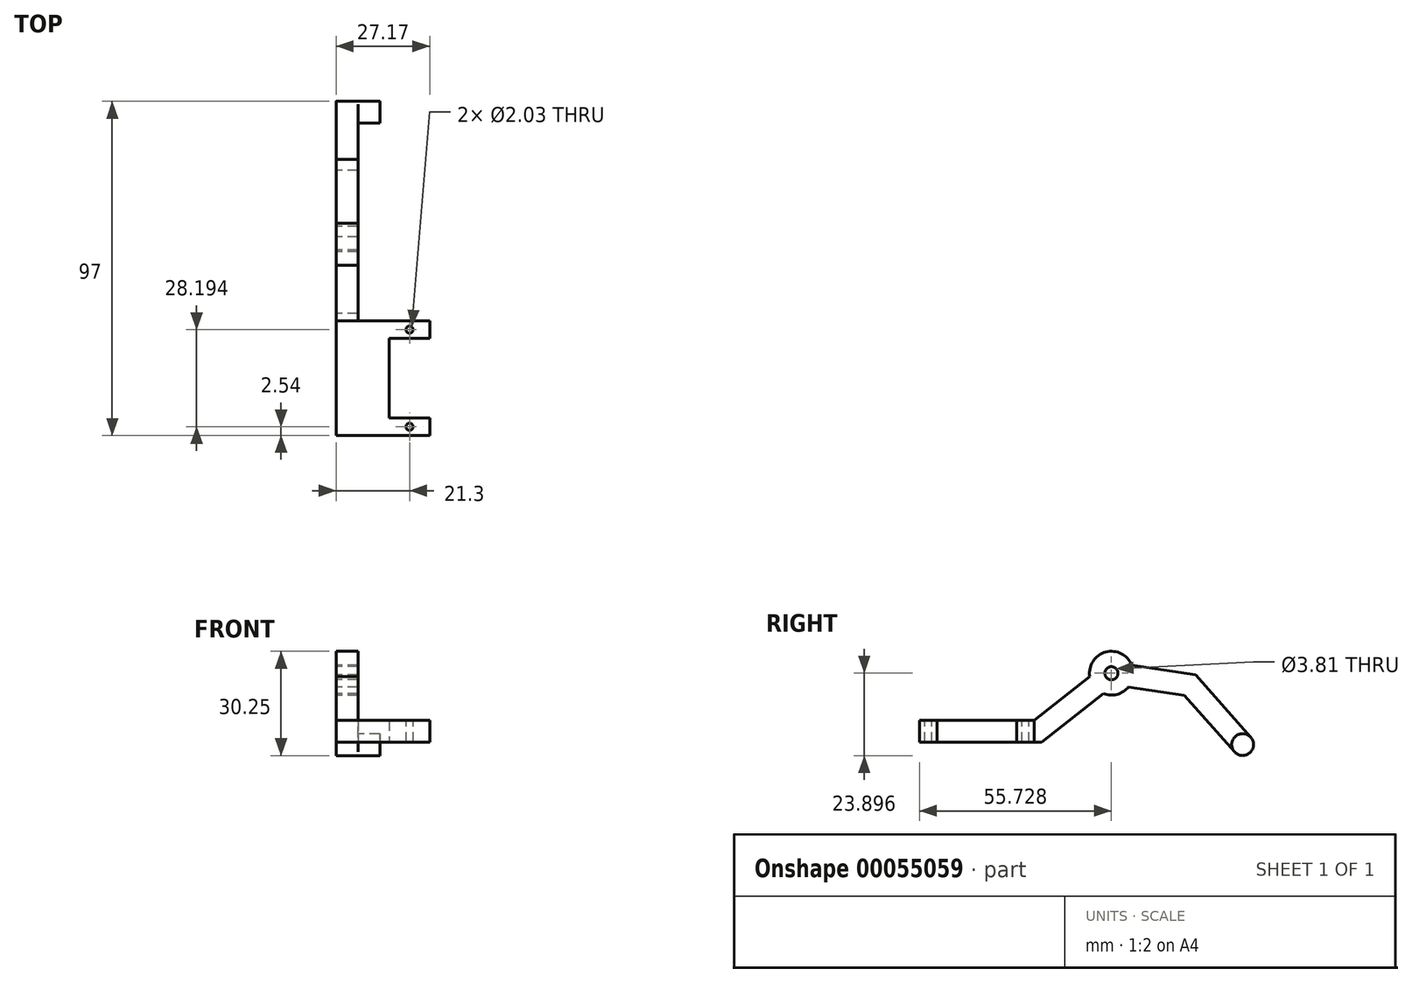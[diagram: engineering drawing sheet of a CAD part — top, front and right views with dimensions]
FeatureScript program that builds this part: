
annotation { "Feature Type Name" : "Feature", "Feature Type Description" : "" }
export const myFeature = defineFeature(function(context is Context, id is Id, definition is map)
    precondition{}
    {
        {
            var Q0;
            Q0=qCreatedBy(makeId("Right.planeOp"),FACE);
            var sketch = newSketch(context, id + "F0", { "sketchPlane" : qUnion([Q0])});
            skLineSegment(sketch, "E0", {"start": v(0, 0) * mm, "end": v(0, 6.35) * mm});
            skLineSegment(sketch, "E1", {"start": v(0, 0) * mm, "end": v(35.48, 0) * mm});
            skLineSegment(sketch, "E2", {"start": v(35.48, 0) * mm, "end": v(53.38, 14.16) * mm});
            skArc(sketch, "E3", {"start": v(53.38, 14.16) * mm, "mid": v(57.36, 13.93) * mm, "end": v(60.7, 16.11) * mm});
            skLineSegment(sketch, "E4", {"start": v(0, 6.35) * mm, "end": v(33.27, 6.35) * mm});
            skLineSegment(sketch, "E5", {"start": v(33.27, 6.35) * mm, "end": v(49.44, 19.14) * mm});
            skLineSegment(sketch, "E6", {"start": v(60.7, 16.11) * mm, "end": v(76.93, 13.67) * mm});
            skLineSegment(sketch, "E7", {"start": v(91.45, -2.75) * mm, "end": v(76.93, 13.67) * mm});
            skArc(sketch, "E8", {"start": v(91.45, -2.75) * mm, "mid": v(95.93, -3.03) * mm, "end": v(96.2, 1.45) * mm});
            skLineSegment(sketch, "E9", {"start": v(61.64, 22.39) * mm, "end": v(80.16, 19.6) * mm});
            skLineSegment(sketch, "E10", {"start": v(96.2, 1.45) * mm, "end": v(80.16, 19.6) * mm});
            skArc(sketch, "E11.trimOffspring", {"start": v(61.64, 22.39) * mm, "mid": v(54.1, 26.2) * mm, "end": v(49.44, 19.14) * mm});
            skLineSegment(sketch, "E12", {"start": v(5.08, 6.35) * mm, "end": v(5.08, 0) * mm, "construction": true});
            skLineSegment(sketch, "E13", {"start": v(28.2, 6.35) * mm, "end": v(28.2, 0) * mm, "construction": true});
            skLineSegment(sketch, "E14", {"start": v(55.73, 20.07) * mm, "end": v(78.55, 16.64) * mm, "construction": true});
            skLineSegment(sketch, "E15", {"start": v(78.55, 16.64) * mm, "end": v(93.83, -0.65) * mm, "construction": true});
            skLineSegment(sketch, "E16", {"start": v(60.7, 16.11) * mm, "end": v(61.64, 22.39) * mm, "construction": true});
            skPoint(sketch, "E17", {"position": v(61.17, 19.25) * mm});
            skLineSegment(sketch, "E18", {"start": v(91.45, -2.75) * mm, "end": v(96.2, 1.45) * mm, "construction": true});
            skLineSegment(sketch, "E19", {"start": v(49.44, 19.14) * mm, "end": v(53.38, 14.16) * mm, "construction": true});
            skLineSegment(sketch, "E20", {"start": v(51.41, 16.65) * mm, "end": v(55.73, 20.07) * mm, "construction": true});
            skCircle(sketch, "E21", {"center": v(55.73, 20.07) * mm, "radius": 1.9 * mm});
            skSolve(sketch);
        }
        {
            var Q0;
            Q0=makeQuery(id+"F0.imprint","IMPRINT",FACE,{"disambiguationData":[TD([[makeQuery(id+"F0.imprint","IMPRINT",EDGE,{"derivedFrom":sQuery(id+"F0.wireOp",EDGE,"E0")}),-1.0]])]});
            extrude(context, id + "F1", {"entities" : qUnion([Q0]), "depth" : 6.35 * mm});
        }
        {
            var Q0;
            {var subQ0=sQuery(id+"F0.wireOp",EDGE,"E9");var subQ1=sQuery(id+"F0.wireOp",EDGE,"E7");var subQ2=sQuery(id+"F0.wireOp",EDGE,"E6");var subQ3=sQuery(id+"F0.wireOp",EDGE,"E5");var subQ4=sQuery(id+"F0.wireOp",EDGE,"E8");var subQ5=sQuery(id+"F0.wireOp",EDGE,"E1");var subQ6=sQuery(id+"F0.wireOp",EDGE,"E2");var subQ7=sQuery(id+"F0.wireOp",EDGE,"E10");var subQ8=sQuery(id+"F0.wireOp",EDGE,"E3");var subQ9=sQuery(id+"F0.wireOp",EDGE,"E4");var subQ10=sQuery(id+"F0.wireOp",EDGE,"E11.trimOffspring");Q0=makeQuery(id+"FnFxDPICjbSdQn6_1.boolean.opBoolean","SPLIT",FACE,{"disambiguationData":[TD([makeQuery(id+"F1.opExtrude","SWEPT_FACE",FACE,{"disambiguationData":[OSD([subQ6])]})])],"derivedFrom":makeQuery(id+"F1.opExtrude","CAP_FACE",FACE,{"disambiguationData":[OSD([sQuery(id+"F0.wireOp",EDGE,"E0"),subQ5,subQ6,subQ8,subQ9,subQ3,subQ2,subQ1,subQ4,subQ0,subQ7,subQ10])],"isStart":false})});}
            var sketch = newSketch(context, id + "F2", { "sketchPlane" : qUnion([Q0])});
            skCircle(sketch, "E22", {"center": v(93.83, -0.65) * mm, "radius": 3.18 * mm});
            skSolve(sketch);
        }
        {
            var Q0;
            Q0 = qSketchRegion(id + "F2", true);
            extrude(context, id + "F3", {"entities" : qUnion([Q0]), "operationType" : NewBodyOperationType.ADD, "depth" : 6.35 * mm});
        }
        {
            var Q0;
            Q0=makeQuery(id+"F1.opExtrude","CAP_FACE",FACE,{"disambiguationData":[OSD([sQuery(id+"F0.wireOp",EDGE,"E0"),sQuery(id+"F0.wireOp",EDGE,"E1"),sQuery(id+"F0.wireOp",EDGE,"E2"),sQuery(id+"F0.wireOp",EDGE,"E3"),sQuery(id+"F0.wireOp",EDGE,"E4"),sQuery(id+"F0.wireOp",EDGE,"E5"),sQuery(id+"F0.wireOp",EDGE,"E6"),sQuery(id+"F0.wireOp",EDGE,"E7"),sQuery(id+"F0.wireOp",EDGE,"E8"),sQuery(id+"F0.wireOp",EDGE,"E9"),sQuery(id+"F0.wireOp",EDGE,"E10"),sQuery(id+"F0.wireOp",EDGE,"E11.trimOffspring"),sQuery(id+"F0.wireOp",EDGE,"E21")])],"isStart":false});
            var sketch = newSketch(context, id + "F4", { "sketchPlane" : qUnion([Q0])});
            skLineSegment(sketch, "E23.bottom", {"start": v(0, 6.35) * mm, "end": v(33.27, 6.35) * mm});
            skLineSegment(sketch, "E23.top", {"start": v(0, 0) * mm, "end": v(33.27, 0) * mm});
            skLineSegment(sketch, "E23.left", {"start": v(0, 6.35) * mm, "end": v(0, 0) * mm});
            skLineSegment(sketch, "E23.right", {"start": v(33.27, 6.35) * mm, "end": v(33.27, 0) * mm});
            skSolve(sketch);
        }
        {
            var Q0;
            Q0=makeQuery(id+"F4.imprint","IMPRINT",FACE,{"disambiguationData":[TD([[makeQuery(id+"F4.imprint","IMPRINT",EDGE,{"derivedFrom":sQuery(id+"F4.wireOp",EDGE,"E23.bottom")}),-1.0]])]});
            extrude(context, id + "F5", {"entities" : qUnion([Q0]), "operationType" : NewBodyOperationType.ADD, "depth" : 9.08 * mm});
        }
        {
            var Q0;
            Q0=makeQuery(id+"F5.opExtrude","CAP_FACE",FACE,{"disambiguationData":[OSD([sQuery(id+"F4.wireOp",EDGE,"E23.bottom"),sQuery(id+"F4.wireOp",EDGE,"E23.top"),sQuery(id+"F4.wireOp",EDGE,"E23.left"),sQuery(id+"F4.wireOp",EDGE,"E23.right")])],"isStart":false});
            var sketch = newSketch(context, id + "F6", { "sketchPlane" : qUnion([Q0])});
            skLineSegment(sketch, "E24.bottom", {"start": v(0, 6.35) * mm, "end": v(5.08, 6.35) * mm});
            skLineSegment(sketch, "E24.top", {"start": v(0, 0) * mm, "end": v(5.08, 0) * mm});
            skLineSegment(sketch, "E24.left", {"start": v(0, 6.35) * mm, "end": v(0, 0) * mm});
            skLineSegment(sketch, "E24.right", {"start": v(5.08, 6.35) * mm, "end": v(5.08, 0) * mm});
            skLineSegment(sketch, "E25.bottom", {"start": v(28.2, 6.35) * mm, "end": v(33.27, 6.35) * mm});
            skLineSegment(sketch, "E25.top", {"start": v(28.2, 0) * mm, "end": v(33.27, 0) * mm});
            skLineSegment(sketch, "E25.left", {"start": v(28.2, 6.35) * mm, "end": v(28.2, 0) * mm});
            skLineSegment(sketch, "E25.right", {"start": v(33.27, 6.35) * mm, "end": v(33.27, 0) * mm});
            skSolve(sketch);
        }
        {
            var Q0;
            Q0 = qSketchRegion(id + "F6", true);
            extrude(context, id + "F7", {"entities" : qUnion([Q0]), "operationType" : NewBodyOperationType.ADD, "depth" : 11.73 * mm});
        }
        {
            var Q0;
            Q0=makeQuery(id+"F7.boolean.opBoolean","MERGE",FACE,{"derivedFrom":[makeQuery(id+"F5.boolean.opBoolean","MERGE",FACE,{"derivedFrom":[makeQuery(id+"F1.opExtrude","SWEPT_FACE",FACE,{"disambiguationData":[OSD([sQuery(id+"F0.wireOp",EDGE,"E4")])]}),makeQuery(id+"F5.opExtrude","SWEPT_FACE",FACE,{"disambiguationData":[OSD([sQuery(id+"F4.wireOp",EDGE,"E23.bottom")])]})]}),makeQuery(id+"F7.opExtrude","SWEPT_FACE",FACE,{"disambiguationData":[OSD([sQuery(id+"F6.wireOp",EDGE,"E24.bottom")])]}),makeQuery(id+"F7.opExtrude","SWEPT_FACE",FACE,{"disambiguationData":[OSD([sQuery(id+"F6.wireOp",EDGE,"E25.bottom")])]})]});
            var sketch = newSketch(context, id + "F8", { "sketchPlane" : qUnion([Q0])});
            skCircle(sketch, "E26", {"center": v(21.3, 30.73) * mm, "radius": 1.02 * mm});
            skCircle(sketch, "E27", {"center": v(21.3, 2.54) * mm, "radius": 1.02 * mm});
            skPoint(sketch, "E28", {"position": v(21.3, 28.2) * mm});
            skPoint(sketch, "E29", {"position": v(27.17, 30.73) * mm});
            skPoint(sketch, "E30", {"position": v(27.17, 2.54) * mm});
            skSolve(sketch);
        }
        {
            var Q0;
            Q0 = qSketchRegion(id + "F8", true);
            extrude(context, id + "F9", {"entities" : qUnion([Q0]), "operationType" : NewBodyOperationType.REMOVE, "endBound" : BoundingType.UP_TO_NEXT, "oppositeDirection" : true, "depth" : 25.4 * mm});
        }
    });
